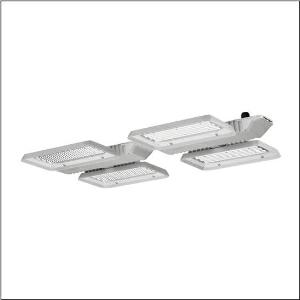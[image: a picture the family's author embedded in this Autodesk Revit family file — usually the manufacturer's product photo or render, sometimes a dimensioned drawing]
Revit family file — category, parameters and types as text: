
# Revit family: highbay_11_51hla1d24mca
name_source: partatom
category: Lighting Fixtures
units: mm (PartAtom-declared; Revit-internal decimal feet)

## family parameters
Cut with Voids When Loaded = No
Host = Face
Light Source = No
Part Type = Normal
Room Calculation Point = No
Round Connector Dimension = Use Diameter
Shared = No

## types (1)
- --- (1 x LED, 28120 lm, 162.4 W, 4000K)
    Apparent Load = 162 VA
    CIE Flux Codes = 88 95 99 100 99
    Color Rendering = 80
    Color Temperature = 4000K
    Default Elevation = 1800 mm
    Description = Highbay 11, LED high bay luminaire, primary light control with lens, of PMMA, light emission: direct distribution, primary light characteristic: symmetric, installation type: suspended mounting, surface-mounted, for 2x 2x LED, rated luminous flux: 28.120lm, luminous efficacy: 173lm/W, light colour: 840, colour temperature: 4000K, control gear: ECG DALI, with terminal, 5-pole, max. 2.5mm², mains connection: 230..240V, AC, 50/60Hz, rated input power: 162W, LED unit, of diecast aluminium, unplated, bead blasted, silver, length: 940mm, width: 500mm, height: 65mm, housing, of diecast aluminium, uncoated, bead blasted, silver, protection rating (complete): IP65, insulation class (complete): insulation class I (protective earthing), certification: CE, ENEC, VDE, UKCA, protection symbol: D, impact resistance: IK08 with glass or PC cover, permissible operating ambient temperature: -35..+55°C, reducing of maximum allowable ambient temperature of 5°C with ceiling mounting, corresponds to IFS (International Featured Standards) requirements for safety and quality in the food industry, packaging unit: 1 piece
    Height = 95 mm
    Lamp = 1 x LED
    Lamp Light Flux = 28120 lm
    Lamp Power = 162.4 W
    Lamp count = 1
    Length = 939 mm
    Luminous efficacy = 173 lm/W
    Manufacturer = Siteco
    ModVariant = No
    Model = 51HLA1D24MCA
    Mounting Place = Ceiling
    Mounting Type = Pendant
    Number of Poles = 1
    OnlyDefault = Yes
    Power Factor = 1
    Product Name = Highbay 11
    Product group = LED high bay luminaire
    ProductGroupID = 903
    Protection Class = Protection class I
    Protection Degree = IP 65
    RLX_Detail_Level = 1
    RLX_Emergency_Light_Flux = 0 lm
    RLX_Emergency_Type = 0
    RLX_Emergency_Type_DB = No
    RlxData = <blob elided: 100013 chars, md5=d7ced593>
    Socket = socket
    Standby Power = 0 W
    System Light Flux = 28120 lm
    System Power = 162 W
    Type Comments = factory setting: luminous flux: 100 % | dim-lin: 254 | 460 mA
    Type Image = l_1003428.jpg
    URL = http://relux.com
    VarID = @adj_177629
    Voltage = 0 V
    Weight = 0.00 kg
    Width = 501 mm

## geometry (parser evidence)
native form markers: Blend x4, Sweep x13
no freeform markers — native parametric forms only
